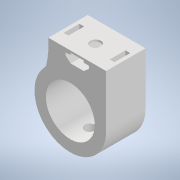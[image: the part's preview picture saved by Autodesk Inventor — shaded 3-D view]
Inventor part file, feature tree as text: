
AUTODESK INVENTOR PART (.ipt)
format: ipt  version: 2020.2 (Build 242310000, 310)  size: 199,680 bytes
history: native  units: in
note: dims shown in document units (in); Inventor stores cm internally (conversion verified against a paired STEP export)
features: extrude x5, sketch x3, plane x2, fillet x1
ambient origin geometry x8: Origin, YZ Plane, XZ Plane, XY Plane, X Axis, Y Axis, Z Axis, Center Point
bodies: Body1 (feature_tree)
feature tree (11):
  sketch  "Sketch5"  dims[d0=1.1in d1=1.0in]
  plane  "Work Plane4"
  extrude  "Extrusion7"  Depth=1.0in
  extrude  "Extrusion8"  Depth=0.175in
  extrude  "Extrusion9"  Depth=0.1in
  fillet  "Fillet1"  Radius=0.2in
  extrude  "Extrusion10"  Depth=0.1in TaperAngle=0.0deg
  plane  "Work Plane5"
  extrude  "Extrusion11"  Depth=0.1in TaperAngle=0.0deg
  sketch  "Sketch10"  dims[d2=0.93in d5=0.175in]
  sketch  "Sketch11"  dims[d6=0.45in d7=0.1in d19=0.2in d25=0.75in d26=0.0in d27=0.8in d28=0.0in d29=0.6in d30=0.0in d31=0.125in d32=0.09in d33=0.3in d34=0.1in d35=0.0in d36=0.2in d37=0.6in d38=0.0in]
